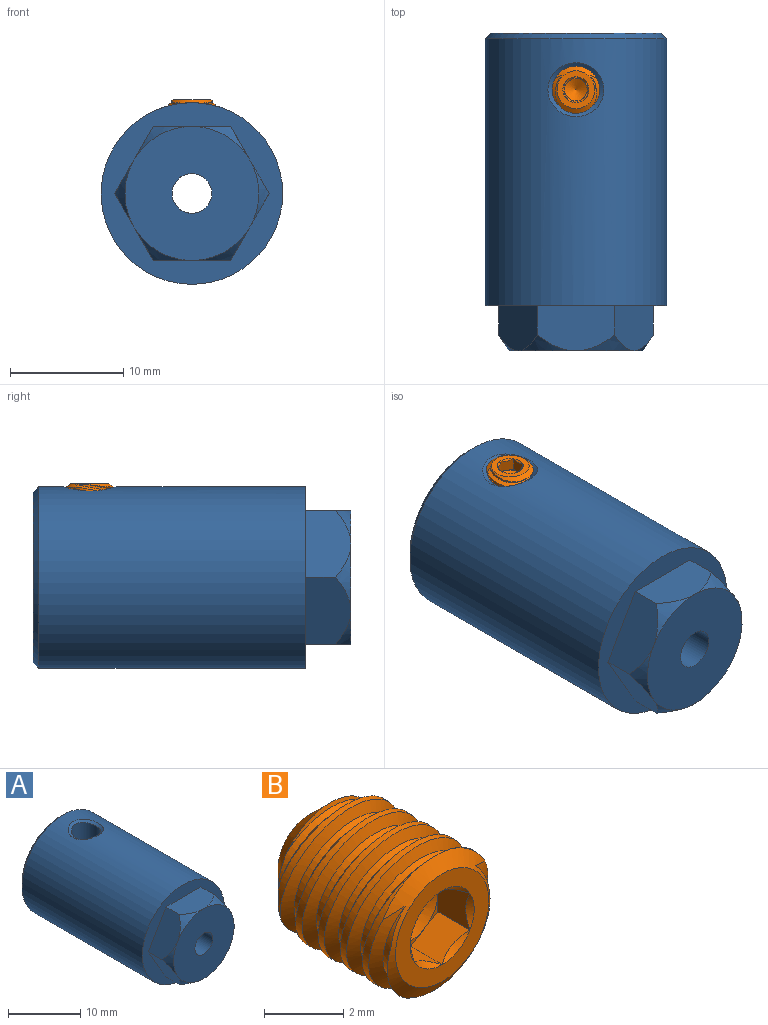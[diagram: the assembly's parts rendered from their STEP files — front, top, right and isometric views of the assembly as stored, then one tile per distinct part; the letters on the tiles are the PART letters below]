
ASSEMBLY  parts=2 mates=1
PART A: 23 faces, bbox 16.8x28.8x16.8 mm
  f0: bspline ~4.93x4.75mm, area 7.1mm2, adj f4,f7
  f1: cone r=5.9mm half-angle=33.7deg, axis (0,1,0), area 5.3mm2, adj f14,f15,f16
  f2: cone r=2.38mm half-angle=45deg, axis (0,1,0), area 11.7mm2, adj f6,f9
  f3: cone r=8mm half-angle=45deg, axis (0,-1,0), area 34.4mm2, adj f7,f9
  f4: cylinder r=2mm len=5.34mm, axis (0,0,-1), area 67.1mm2, adj f0,f6
  f5: cylinder r=1.75mm len=8mm, axis (0,-1,0), area 88mm2, adj f16,f17
  f6: cylinder r=2.38mm len=19.5mm, axis (0,1,0), area 277.1mm2, adj f2,f4,f17
  f7: cylinder r=8mm len=23.5mm, axis (0,1,0), area 1162.6mm2, adj f0,f3,f8
  f8: plane 16x16mm, normal (0,-1,0), area 80.5mm2, adj f7,f10,f11,f12,f13,f14,f15
  f9: plane 15x15mm, normal (0,1,0), area 150.7mm2, adj f2,f3
  f10: plane 7.62x4.8mm, normal (0,0,-1), area 24mm2, adj f8,f11,f15,f21,f22
  f11: plane 6.7x4.8mm, normal (0.87,0,-0.5), area 24.1mm2, adj f8,f10,f12,f18,f22
  f12: plane 6.7x4.8mm, normal (0.87,0,0.5), area 24mm2, adj f8,f11,f13,f18,f19
  f13: plane 7.62x4.8mm, normal (0,0,1), area 24mm2, adj f8,f12,f14,f19,f20
  f14: plane 6.7x4.8mm, normal (-0.87,0,0.5), area 24.1mm2, adj f1,f8,f13,f15,f20
  f15: plane 6.7x4.8mm, normal (-0.87,0,-0.5), area 24.1mm2, adj f1,f8,f10,f14,f21
  f16: plane 11.8x11.8mm, normal (0,-1,0), area 99.7mm2, adj f1,f5,f18,f19,f20,f21,f22
  f17: plane 4.75x4.75mm, normal (0,1,0), area 8.1mm2, adj f5,f6
  f18: cone r=5.9mm half-angle=33.7deg, axis (0,1,0), area 5.3mm2, adj f11,f12,f16
  f19: cone r=5.9mm half-angle=33.7deg, axis (0,1,0), area 5.3mm2, adj f12,f13,f16
  f20: cone r=5.9mm half-angle=33.7deg, axis (0,1,0), area 5.3mm2, adj f13,f14,f16
  f21: cone r=5.9mm half-angle=33.7deg, axis (0,1,0), area 5.3mm2, adj f10,f15,f16
  f22: cone r=5.9mm half-angle=33.7deg, axis (0,1,0), area 5.3mm2, adj f10,f11,f16
PART B: 47 faces, bbox 4.8x5.3x4.9 mm
  f0: cone r=0.99mm half-angle=59deg, axis (0,-1,0), area 3.6mm2, adj f1,f42,f43,f44,f45,f46
  f1: plane 0.86x0.5mm, normal (0,-1,0), area 0.1mm2, adj f0,f2,f41
  f2: plane 1.26x1.25mm, normal (-1,0,0), area 1.2mm2, adj f1,f3,f40,f41,f42
  f3: plane 1.58x1.43mm, normal (-0.5,0,-0.87), area 1.2mm2, adj f2,f4,f39,f42,f43
  f4: plane 1.58x1.43mm, normal (0.5,0,-0.87), area 1.2mm2, adj f3,f5,f38,f43,f44
  f5: plane 1.58x1.58mm, normal (1,0,0), area 1.2mm2, adj f4,f6,f37,f44,f45
  f6: plane 1.58x1.43mm, normal (0.5,0,0.87), area 1.2mm2, adj f5,f7,f41,f45,f46
  f7: cone r=1.15mm half-angle=45deg, axis (0,-1,0), area 0mm2, adj f6,f8
  f8: plane 3.33x3.33mm, normal (0,-1,0), area 4.6mm2, adj f7,f9,f10,f37,f38,f39,f40
  f9: cone r=1.15mm half-angle=45deg, axis (0,-1,0), area 0mm2, adj f8,f41
  f10: cone r=2.08mm half-angle=55deg, axis (0,1,0), area 4.3mm2, adj f8,f11,f12,f13,f14,f15,f16
  f11: cylinder r=2.08mm len=1.94mm, axis (0,-1,0), area 0mm2, adj f10,f12
  f12: cone r=2.21mm half-angle=60deg, axis (0,-0.98,-0.19), area 1.4mm2, adj f10,f11,f13
  f13: cylinder r=1.78mm len=3.55mm, axis (0,0.98,0.19), area 1.4mm2, adj f10,f12,f14
  f14: cone r=1.78mm half-angle=60deg, axis (0,0.98,0.19), area 3.4mm2, adj f10,f13,f15
  f15: cylinder r=2.08mm len=4.17mm, axis (0,-1,0), area 2.1mm2, adj f10,f14,f16
  f16: cone r=2.21mm half-angle=60deg, axis (0,-0.98,-0.19), area 5mm2, adj f10,f15,f17
  f17: cylinder r=1.78mm len=3.55mm, axis (0,0.98,0.19), area 2.2mm2, adj f16,f18
  f18: cone r=1.78mm half-angle=60deg, axis (0,0.98,0.19), area 4.8mm2, adj f17,f19
  f19: cylinder r=2.08mm len=4.17mm, axis (0,-1,0), area 2.7mm2, adj f18,f20
  f20: cone r=2.21mm half-angle=60deg, axis (0,-0.98,-0.19), area 5mm2, adj f19,f21
  f21: cylinder r=1.78mm len=3.55mm, axis (0,0.98,0.19), area 2.2mm2, adj f20,f22
  f22: cone r=1.78mm half-angle=60deg, axis (0,0.98,0.19), area 4.8mm2, adj f21,f23
  f23: cylinder r=2.08mm len=4.17mm, axis (0,-1,0), area 2.7mm2, adj f22,f24
  f24: cone r=2.21mm half-angle=60deg, axis (0,-0.98,-0.19), area 5mm2, adj f23,f25
  f25: cylinder r=1.78mm len=3.55mm, axis (0,0.98,0.19), area 2.2mm2, adj f24,f26
  f26: cone r=1.78mm half-angle=60deg, axis (0,0.98,0.19), area 4.8mm2, adj f25,f27
  f27: cylinder r=2.08mm len=4.17mm, axis (0,-1,0), area 2.7mm2, adj f26,f28
  f28: cone r=2.21mm half-angle=60deg, axis (0,-0.98,-0.19), area 5mm2, adj f27,f29
  f29: cylinder r=1.78mm len=3.55mm, axis (0,0.98,0.19), area 2.2mm2, adj f28,f30
  f30: cone r=1.78mm half-angle=60deg, axis (0,0.98,0.19), area 4mm2, adj f29,f31,f36
  f31: cone r=1.1mm half-angle=45deg, axis (0,-1,0), area 11mm2, adj f30,f32,f33,f34,f35,f36
  f32: cone r=1.78mm half-angle=60deg, axis (0,0.98,0.19), area 0.2mm2, adj f31,f33
  f33: cylinder r=1.78mm len=3.55mm, axis (0,0.98,0.19), area 0.9mm2, adj f31,f32,f34
  f34: cone r=2.21mm half-angle=60deg, axis (0,-0.98,-0.19), area 2.1mm2, adj f31,f33,f36
  f35: cone r=1664.28mm half-angle=59deg, axis (0,1,0), area 4.5mm2, adj f31
  f36: cylinder r=2.08mm len=4.17mm, axis (0,-1,0), area 2mm2, adj f30,f31,f34
  f37: cone r=1.15mm half-angle=45deg, axis (0,-1,0), area 0mm2, adj f5,f8
  f38: cone r=1.15mm half-angle=45deg, axis (0,-1,0), area 0mm2, adj f4,f8
  f39: cone r=1.15mm half-angle=45deg, axis (0,-1,0), area 0mm2, adj f3,f8
  f40: cone r=1.15mm half-angle=45deg, axis (0,-1,0), area 0.1mm2, adj f2,f8
  f41: plane 1.58x1.43mm, normal (-0.5,0,0.87), area 1.2mm2, adj f1,f2,f6,f9,f46
  f42: plane 0.86x0.5mm, normal (0,-1,0), area 0.1mm2, adj f0,f2,f3
  f43: plane 0.99x0.29mm, normal (0,-1,0), area 0.1mm2, adj f0,f3,f4
  f44: plane 0.86x0.5mm, normal (0,-1,0), area 0.1mm2, adj f0,f4,f5
  f45: plane 0.86x0.5mm, normal (0,-1,0), area 0.1mm2, adj f0,f5,f6
  f46: plane 0.99x0.29mm, normal (0,-1,0), area 0.1mm2, adj f0,f6,f41
PLACE A t=(-4.05,14.23,-20.47)mm
PLACE B rot(axis=(-1,0,0),90deg) t=(0,0,2.71)mm
MATE fastened B.f35 <-> A.f4  axis (0,0,1) through (0,0,4.76)mm
